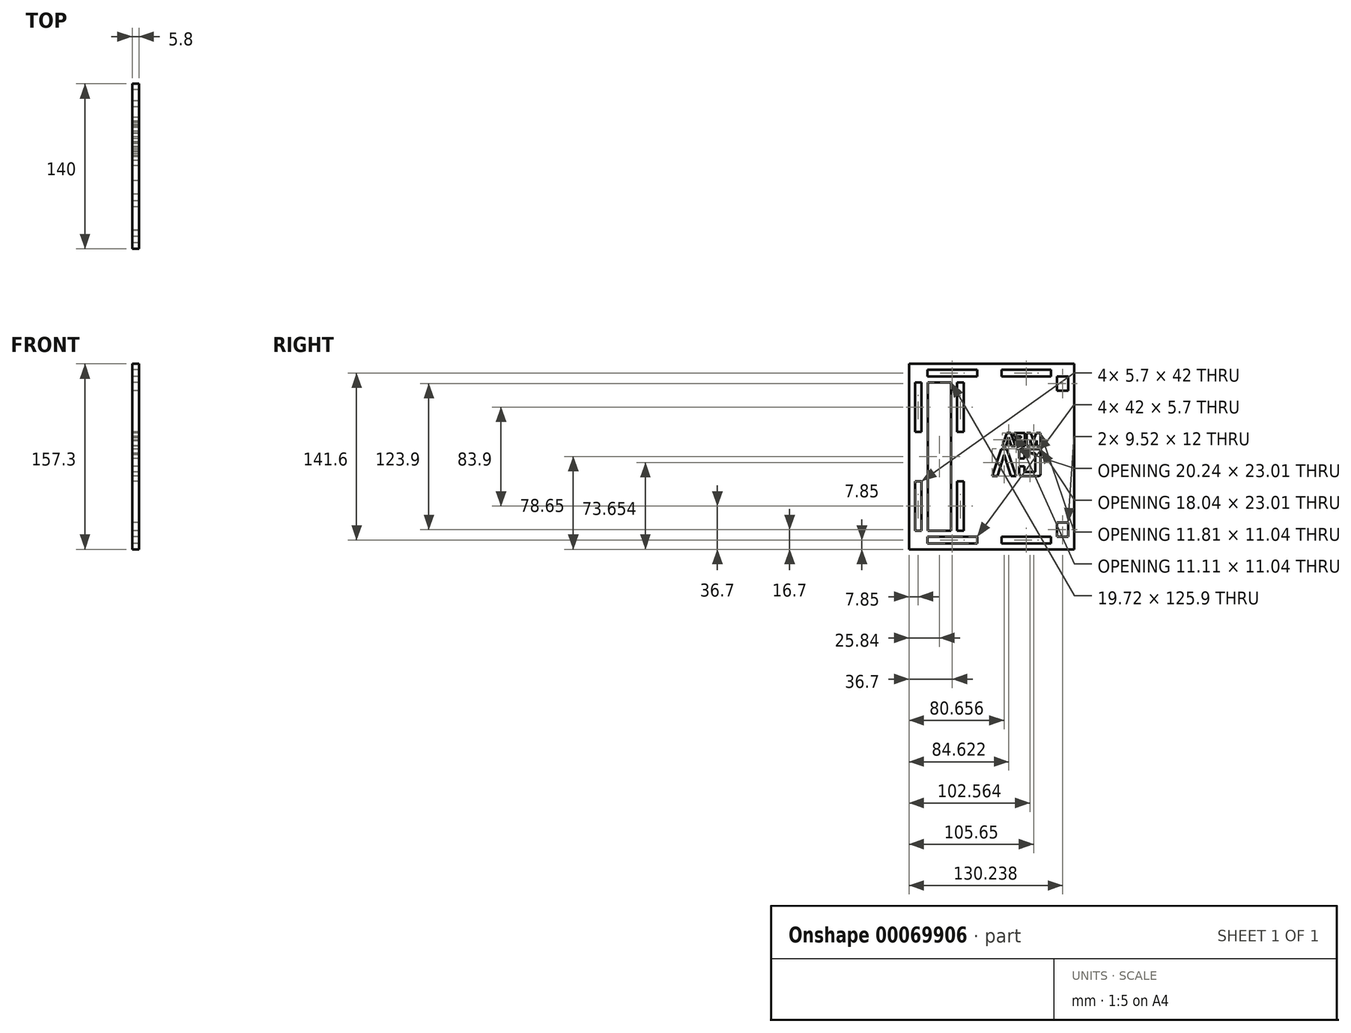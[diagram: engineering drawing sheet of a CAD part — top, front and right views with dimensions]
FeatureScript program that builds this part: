
annotation { "Feature Type Name" : "Feature", "Feature Type Description" : "" }
export const myFeature = defineFeature(function(context is Context, id is Id, definition is map)
    precondition{}
    {
        {
            var Q0;
            Q0=qCreatedBy(makeId("Right.planeOp"),FACE);
            var sketch = newSketch(context, id + "F0", { "sketchPlane" : qUnion([Q0])});
            skLineSegment(sketch, "E0.bottom", {"start": v(70, 78.65) * mm, "end": v(-70, 78.65) * mm});
            skLineSegment(sketch, "E0.top", {"start": v(70, -78.65) * mm, "end": v(-70, -78.65) * mm});
            skLineSegment(sketch, "E0.left", {"start": v(70, 78.65) * mm, "end": v(70, -78.65) * mm});
            skLineSegment(sketch, "E0.right", {"start": v(-70, 78.65) * mm, "end": v(-70, -78.65) * mm});
            skPoint(sketch, "E0.middle", {"position": v(0, 0) * mm});
            skLineSegment(sketch, "E1", {"start": v(-65, 78.65) * mm, "end": v(-65, -78.65) * mm, "construction": true});
            skLineSegment(sketch, "E2", {"start": v(-59.3, 78.65) * mm, "end": v(-59.3, -78.65) * mm, "construction": true});
            skLineSegment(sketch, "E3", {"start": v(-23.6, -78.65) * mm, "end": v(-23.6, 78.65) * mm, "construction": true});
            skLineSegment(sketch, "E4", {"start": v(-29.3, -78.65) * mm, "end": v(-29.3, 78.65) * mm, "construction": true});
            skLineSegment(sketch, "E5", {"start": v(-70, 73.65) * mm, "end": v(70, 73.65) * mm, "construction": true});
            skLineSegment(sketch, "E6", {"start": v(-70, 67.95) * mm, "end": v(70, 67.95) * mm, "construction": true});
            skLineSegment(sketch, "E7", {"start": v(-70, -67.95) * mm, "end": v(70, -67.95) * mm, "construction": true});
            skLineSegment(sketch, "E8", {"start": v(-70, -73.65) * mm, "end": v(70, -73.65) * mm, "construction": true});
            skLineSegment(sketch, "E9.bottom", {"start": v(-65, 20.95) * mm, "end": v(-59.3, 20.95) * mm});
            skLineSegment(sketch, "E9.top", {"start": v(-65, 62.95) * mm, "end": v(-59.3, 62.95) * mm});
            skLineSegment(sketch, "E9.left", {"start": v(-65, 20.95) * mm, "end": v(-65, 62.95) * mm});
            skLineSegment(sketch, "E9.right", {"start": v(-59.3, 20.95) * mm, "end": v(-59.3, 62.95) * mm});
            skLineSegment(sketch, "E10.bottom", {"start": v(-65, -62.95) * mm, "end": v(-59.3, -62.95) * mm});
            skLineSegment(sketch, "E10.top", {"start": v(-65, -20.95) * mm, "end": v(-59.3, -20.95) * mm});
            skLineSegment(sketch, "E10.left", {"start": v(-65, -62.95) * mm, "end": v(-65, -20.95) * mm});
            skLineSegment(sketch, "E10.right", {"start": v(-59.3, -62.95) * mm, "end": v(-59.3, -20.95) * mm});
            skLineSegment(sketch, "E11", {"start": v(65, 78.65) * mm, "end": v(65, -78.65) * mm, "construction": true});
            skLineSegment(sketch, "E12", {"start": v(-59.3, 62.95) * mm, "end": v(-23.6, 62.95) * mm, "construction": true});
            skLineSegment(sketch, "E13", {"start": v(-59.3, -62.95) * mm, "end": v(-23.6, -62.95) * mm, "construction": true});
            skLineSegment(sketch, "E14.bottom", {"start": v(-29.3, 62.95) * mm, "end": v(-23.6, 62.95) * mm, "construction": true});
            skLineSegment(sketch, "E14.top", {"start": v(-29.3, 20.95) * mm, "end": v(-23.6, 20.95) * mm, "construction": true});
            skLineSegment(sketch, "E14.left", {"start": v(-29.3, 62.95) * mm, "end": v(-29.3, 20.95) * mm, "construction": true});
            skLineSegment(sketch, "E14.right", {"start": v(-23.6, 62.95) * mm, "end": v(-23.6, 20.95) * mm, "construction": true});
            skLineSegment(sketch, "E15.bottom", {"start": v(-23.6, -62.95) * mm, "end": v(-29.3, -62.95) * mm, "construction": true});
            skLineSegment(sketch, "E15.top", {"start": v(-23.6, -20.95) * mm, "end": v(-29.3, -20.95) * mm, "construction": true});
            skLineSegment(sketch, "E15.left", {"start": v(-23.6, -62.95) * mm, "end": v(-23.6, -20.95) * mm, "construction": true});
            skLineSegment(sketch, "E15.right", {"start": v(-29.3, -62.95) * mm, "end": v(-29.3, -20.95) * mm, "construction": true});
            skLineSegment(sketch, "E16.bottom", {"start": v(-29.3, 62.95) * mm, "end": v(-23.6, 62.95) * mm});
            skLineSegment(sketch, "E16.top", {"start": v(-29.3, 20.95) * mm, "end": v(-23.6, 20.95) * mm});
            skLineSegment(sketch, "E16.left", {"start": v(-29.3, 62.95) * mm, "end": v(-29.3, 20.95) * mm});
            skLineSegment(sketch, "E16.right", {"start": v(-23.6, 62.95) * mm, "end": v(-23.6, 20.95) * mm});
            skLineSegment(sketch, "E17.bottom", {"start": v(-29.3, -20.95) * mm, "end": v(-23.6, -20.95) * mm});
            skLineSegment(sketch, "E17.top", {"start": v(-29.3, -62.95) * mm, "end": v(-23.6, -62.95) * mm});
            skLineSegment(sketch, "E17.left", {"start": v(-29.3, -20.95) * mm, "end": v(-29.3, -62.95) * mm});
            skLineSegment(sketch, "E17.right", {"start": v(-23.6, -20.95) * mm, "end": v(-23.6, -62.95) * mm});
            skLineSegment(sketch, "E18.bottom", {"start": v(-54.3, 73.65) * mm, "end": v(-12.3, 73.65) * mm});
            skLineSegment(sketch, "E18.top", {"start": v(-54.3, 67.95) * mm, "end": v(-12.3, 67.95) * mm});
            skLineSegment(sketch, "E18.left", {"start": v(-54.3, 73.65) * mm, "end": v(-54.3, 67.95) * mm});
            skLineSegment(sketch, "E18.right", {"start": v(-12.3, 73.65) * mm, "end": v(-12.3, 67.95) * mm});
            skLineSegment(sketch, "E19.bottom", {"start": v(-54.3, -67.95) * mm, "end": v(-12.3, -67.95) * mm});
            skLineSegment(sketch, "E19.top", {"start": v(-54.3, -73.65) * mm, "end": v(-12.3, -73.65) * mm});
            skLineSegment(sketch, "E19.left", {"start": v(-54.3, -67.95) * mm, "end": v(-54.3, -73.65) * mm});
            skLineSegment(sketch, "E19.right", {"start": v(-12.3, -67.95) * mm, "end": v(-12.3, -73.65) * mm});
            skLineSegment(sketch, "E20.bottom", {"start": v(65, 67.95) * mm, "end": v(55.47, 67.95) * mm});
            skLineSegment(sketch, "E20.top", {"start": v(65, 55.95) * mm, "end": v(55.47, 55.95) * mm});
            skLineSegment(sketch, "E20.left", {"start": v(65, 67.95) * mm, "end": v(65, 55.95) * mm});
            skLineSegment(sketch, "E20.right", {"start": v(55.47, 67.95) * mm, "end": v(55.47, 55.95) * mm});
            skLineSegment(sketch, "E21.bottom", {"start": v(65, -67.95) * mm, "end": v(55.47, -67.95) * mm});
            skLineSegment(sketch, "E21.top", {"start": v(65, -55.95) * mm, "end": v(55.47, -55.95) * mm});
            skLineSegment(sketch, "E21.left", {"start": v(65, -67.95) * mm, "end": v(65, -55.95) * mm});
            skLineSegment(sketch, "E21.right", {"start": v(55.48, -67.95) * mm, "end": v(55.48, -55.95) * mm});
            skLineSegment(sketch, "E22.bottom", {"start": v(8.47, 73.65) * mm, "end": v(50.47, 73.65) * mm});
            skLineSegment(sketch, "E22.top", {"start": v(8.47, 67.95) * mm, "end": v(50.48, 67.95) * mm});
            skLineSegment(sketch, "E22.left", {"start": v(8.47, 73.65) * mm, "end": v(8.47, 67.95) * mm});
            skLineSegment(sketch, "E22.right", {"start": v(50.47, 73.65) * mm, "end": v(50.47, 67.95) * mm});
            skLineSegment(sketch, "E23.bottom", {"start": v(8.47, -67.95) * mm, "end": v(50.48, -67.95) * mm});
            skLineSegment(sketch, "E23.top", {"start": v(8.48, -73.65) * mm, "end": v(50.48, -73.65) * mm});
            skLineSegment(sketch, "E23.left", {"start": v(8.47, -67.95) * mm, "end": v(8.47, -73.65) * mm});
            skLineSegment(sketch, "E23.right", {"start": v(50.48, -67.95) * mm, "end": v(50.48, -73.65) * mm});
            skLineSegment(sketch, "E24.bottom", {"start": v(-34.3, 62.95) * mm, "end": v(-54.02, 62.95) * mm});
            skLineSegment(sketch, "E24.top", {"start": v(-34.3, -62.95) * mm, "end": v(-54.02, -62.95) * mm});
            skLineSegment(sketch, "E24.left", {"start": v(-34.3, 62.95) * mm, "end": v(-34.3, -62.95) * mm});
            skLineSegment(sketch, "E24.right", {"start": v(-54.02, 62.95) * mm, "end": v(-54.02, -62.95) * mm});
            skPoint(sketch, "E24.middle", {"position": v(-44.16, 0) * mm});
            skLineSegment(sketch, "E25.MirrorCS", {"start": v(36.94, 9.36) * mm, "end": v(34.31, 9.36) * mm});
            skLineSegment(sketch, "E26.MirrorCS", {"start": v(20.66, 15.77) * mm, "end": v(20.66, 13.25) * mm});
            skLineSegment(sketch, "E27.MirrorCS", {"start": v(34.31, 9.36) * mm, "end": v(32.91, 13.82) * mm});
            skLineSegment(sketch, "E28.MirrorCS", {"start": v(32.91, 13.82) * mm, "end": v(32.91, 8.89) * mm});
            skLineSegment(sketch, "E29.MirrorCS", {"start": v(19.38, 19.93) * mm, "end": v(19.38, 17.27) * mm});
            skLineSegment(sketch, "E30.MirrorCS", {"start": v(32.91, 8.89) * mm, "end": v(29.75, 8.89) * mm});
            skLineSegment(sketch, "E31.MirrorCS", {"start": v(20.66, 13.25) * mm, "end": v(25.02, 13.25) * mm});
            skLineSegment(sketch, "E32.MirrorCS", {"start": v(20.18, 8.92) * mm, "end": v(16.86, 8.89) * mm});
            skLineSegment(sketch, "E33.MirrorCS", {"start": v(25.02, 15.77) * mm, "end": v(20.66, 15.77) * mm});
            skLineSegment(sketch, "E34.MirrorCS", {"start": v(25.02, 13.25) * mm, "end": v(25.02, 8.89) * mm});
            skLineSegment(sketch, "E35.MirrorCS", {"start": v(25.02, 17.27) * mm, "end": v(25.02, 15.77) * mm});
            skLineSegment(sketch, "E36.MirrorCS", {"start": v(25.02, 8.89) * mm, "end": v(28.29, 8.89) * mm});
            skLineSegment(sketch, "E37.MirrorCS", {"start": v(29.75, 19.93) * mm, "end": v(33.19, 19.93) * mm});
            skLineSegment(sketch, "E38.MirrorCS", {"start": v(0.54, -16.44) * mm, "end": v(5.08, -16.5) * mm});
            skLineSegment(sketch, "E39.MirrorCS", {"start": v(12.42, 8.89) * mm, "end": v(9.06, 8.92) * mm});
            skLineSegment(sketch, "E40.MirrorCS", {"start": v(35.6, 14) * mm, "end": v(38.09, 19.93) * mm});
            skLineSegment(sketch, "E41.MirrorCS", {"start": v(19.38, 17.27) * mm, "end": v(25.02, 17.27) * mm});
            skLineSegment(sketch, "E42.MirrorCS", {"start": v(13, 6.5) * mm, "end": v(8.3, 6.5) * mm});
            skLineSegment(sketch, "E43.MirrorCS", {"start": v(12.88, 19.93) * mm, "end": v(16.36, 19.93) * mm});
            skLineSegment(sketch, "E44.MirrorCS", {"start": v(38.35, 13.82) * mm, "end": v(36.94, 9.36) * mm});
            skLineSegment(sketch, "E45.MirrorCS", {"start": v(16.86, 8.89) * mm, "end": v(14.63, 16.4) * mm});
            skLineSegment(sketch, "E46.MirrorCS", {"start": v(39.78, 6.5) * mm, "end": v(25.34, 6.5) * mm});
            skLineSegment(sketch, "E47.MirrorCS", {"start": v(28.29, 8.89) * mm, "end": v(28.29, 19.93) * mm});
            skLineSegment(sketch, "E48.MirrorCS", {"start": v(27.97, -8.25) * mm, "end": v(23.54, -8.25) * mm});
            skLineSegment(sketch, "E49.MirrorCS", {"start": v(27.97, -1.47) * mm, "end": v(27.97, 2.86) * mm});
            skLineSegment(sketch, "E50.MirrorCS", {"start": v(33.19, 19.93) * mm, "end": v(35.6, 14) * mm});
            skLineSegment(sketch, "E51.MirrorCS", {"start": v(16.36, 19.93) * mm, "end": v(20.18, 8.92) * mm});
            skLineSegment(sketch, "E52.MirrorCS", {"start": v(41.55, 8.89) * mm, "end": v(38.35, 8.89) * mm});
            skLineSegment(sketch, "E53.MirrorCS", {"start": v(14.63, 16.4) * mm, "end": v(12.42, 8.89) * mm});
            skLineSegment(sketch, "E54.MirrorCS", {"start": v(23.54, 4.7) * mm, "end": v(23.54, -1.47) * mm});
            skLineSegment(sketch, "E55.MirrorCS", {"start": v(38.09, 19.93) * mm, "end": v(41.55, 19.93) * mm});
            skLineSegment(sketch, "E56.MirrorCS", {"start": v(28.29, 19.93) * mm, "end": v(19.38, 19.93) * mm});
            skLineSegment(sketch, "E57.MirrorCS", {"start": v(16.26, -16.5) * mm, "end": v(20.77, -16.44) * mm});
            skLineSegment(sketch, "E58.MirrorCS", {"start": v(27.97, -12.86) * mm, "end": v(27.97, -8.25) * mm});
            skLineSegment(sketch, "E59.MirrorCS", {"start": v(23.54, -1.47) * mm, "end": v(27.97, -1.47) * mm});
            skLineSegment(sketch, "E60.MirrorCS", {"start": v(38.35, 8.89) * mm, "end": v(38.35, 13.82) * mm});
            skLineSegment(sketch, "E61.MirrorCS", {"start": v(29.75, 8.89) * mm, "end": v(29.75, 19.93) * mm});
            skLineSegment(sketch, "E62.MirrorCS", {"start": v(9.06, 8.92) * mm, "end": v(12.88, 19.93) * mm});
            skLineSegment(sketch, "E63.MirrorCS", {"start": v(41.55, 19.93) * mm, "end": v(41.55, 8.89) * mm});
            skLineSegment(sketch, "E64.MirrorCS", {"start": v(5.08, -16.5) * mm, "end": v(10.69, 1.48) * mm});
            skLineSegment(sketch, "E65.MirrorCS", {"start": v(25.34, -16.5) * mm, "end": v(39.78, -16.5) * mm});
            skLineSegment(sketch, "E66.MirrorCS", {"start": v(37.16, -12.86) * mm, "end": v(27.97, -12.86) * mm});
            skLineSegment(sketch, "E67.MirrorCS", {"start": v(8.3, 6.5) * mm, "end": v(0.54, -16.44) * mm});
            skLineSegment(sketch, "E68.MirrorCS", {"start": v(20.77, -16.44) * mm, "end": v(13, 6.5) * mm});
            skLineSegment(sketch, "E69.MirrorCS", {"start": v(10.69, 1.48) * mm, "end": v(16.26, -16.5) * mm});
            skLineSegment(sketch, "E70.MirrorCS", {"start": v(37.16, 2.86) * mm, "end": v(37.16, -12.86) * mm});
            skLineSegment(sketch, "E71.MirrorCS", {"start": v(27.97, 2.86) * mm, "end": v(37.16, 2.86) * mm});
            skLineSegment(sketch, "E72.MirrorCS", {"start": v(23.54, -8.25) * mm, "end": v(23.54, -14.7) * mm});
            skLineSegment(sketch, "E73.MirrorCS", {"start": v(41.58, -14.7) * mm, "end": v(41.58, 4.7) * mm});
            skPoint(sketch, "E74.visualSharp", {"position": v(23.54, 6.5) * mm});
            skArc(sketch, "E74.filletArc", {"start": v(25.34, 6.5) * mm, "mid": v(24.07, 5.98) * mm, "end": v(23.54, 4.7) * mm});
            skPoint(sketch, "E75.visualSharp", {"position": v(41.58, 6.5) * mm});
            skArc(sketch, "E75.filletArc", {"start": v(41.58, 4.7) * mm, "mid": v(41.06, 5.98) * mm, "end": v(39.78, 6.5) * mm});
            skPoint(sketch, "E76.visualSharp", {"position": v(41.58, -16.5) * mm});
            skArc(sketch, "E76.filletArc", {"start": v(39.78, -16.5) * mm, "mid": v(41.06, -15.97) * mm, "end": v(41.58, -14.7) * mm});
            skPoint(sketch, "E77.visualSharp", {"position": v(23.54, -16.5) * mm});
            skArc(sketch, "E77.filletArc", {"start": v(23.54, -14.7) * mm, "mid": v(24.07, -15.97) * mm, "end": v(25.34, -16.5) * mm});
            skSolve(sketch);
        }
        {
            var Q0;
            Q0=makeQuery(id+"F0.imprint","IMPRINT",FACE,{"disambiguationData":[TD([[makeQuery(id+"F0.imprint","IMPRINT",EDGE,{"derivedFrom":sQuery(id+"F0.wireOp",EDGE,"E0.bottom")}),1.0]])]});
            extrude(context, id + "F1", {"entities" : qUnion([Q0]), "depth" : 5.8 * mm});
        }
    });
